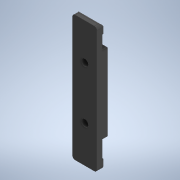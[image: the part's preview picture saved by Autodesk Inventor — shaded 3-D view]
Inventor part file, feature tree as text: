
AUTODESK INVENTOR PART (.ipt)
format: ipt  version: 2021.5 (Build 255421000, 421)  size: 145,408 bytes
history: native  units: mm
features: extrude x3, other x1, sketch x1, fillet x1
ambient origin geometry x8: Origin, YZ Plane, XZ Plane, XY Plane, X Axis, Y Axis, Z Axis, Center Point
bodies: Body1 (feature_tree)
feature tree (6):
  other  "Sólido1"
  sketch  "Boceto1"  dims[d1=4.0mm d2=4.0mm d3=35.0mm d4=72.2mm d5=13.0mm d6=17.0mm d7=23.0mm d8=5.0mm d9=7.0mm d10=9.5mm d11=9.75mm d12=15.0mm d13=4.0mm d14=8.0mm d15=14.0mm d16=72.0mm d17=3.0mm d18=0.0mm d19=3.0mm d20=0.0mm d23=5.0mm d24=0.6mm d25=0.0mm d26=1.5mm]
  extrude  "base"  Depth=1.5mm
  extrude  "base2"  Depth=14.0mm
  extrude  "Extrusión3"  Depth=72.0mm
  fillet  "Empalme2"  Radius=3.0mm
